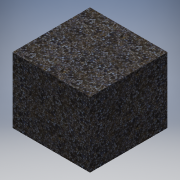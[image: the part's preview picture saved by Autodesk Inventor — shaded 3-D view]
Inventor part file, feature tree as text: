
AUTODESK INVENTOR PART (.ipt)
format: ipt  version: 2016 (Build 200138000, 138)  size: 140,800 bytes
history: native  units: in
note: dims shown in document units (in); Inventor stores cm internally (conversion verified against a paired STEP export)
features: extrude x2, sketch x2
ambient origin geometry x8: Origin, YZ Plane, XZ Plane, XY Plane, X Axis, Y Axis, Z Axis, Center Point
bodies: Solid1 (feature_tree), Solid2 (feature_tree)
feature tree (4):
  extrude  "Extrusion1"  Depth=10.0in
  extrude  "Extrusion2"  Depth=11.811in
  sketch  "Sketch1"  dims[d2=10.0in d3=0.0in d5=5.9055in]
  sketch  "Sketch2"  dims[d6=5.9055in d7=11.811in d8=11.811in d9=11.811in d10=1.1811in d11=0.3937in d12=0.0in]
